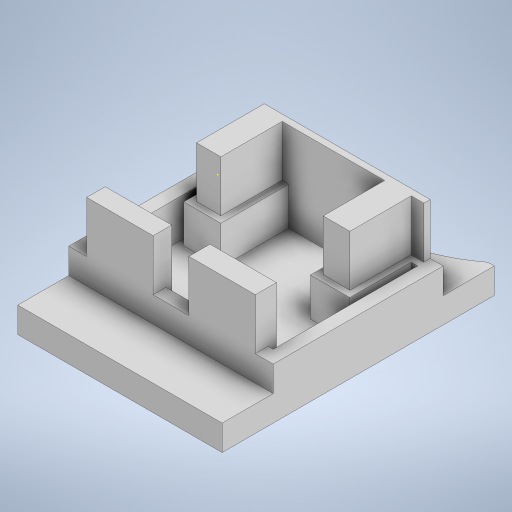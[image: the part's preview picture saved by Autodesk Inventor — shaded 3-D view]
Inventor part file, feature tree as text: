
AUTODESK INVENTOR PART (.ipt)
format: ipt  version: 2024 (Build 280153000, 153)  size: 340,480 bytes
history: native  units: mm
features: extrude x6, sketch x6, projected_geometry x1
ambient origin geometry x8: Origin, YZ Plane, XZ Plane, XY Plane, X Axis, Y Axis, Z Axis, Center Point
bodies: Solid1 (feature_tree)
feature tree (13):
  extrude  "Extrusion1"  Depth=160.0mm
  extrude  "Extrusion2"  Depth=25.0mm
  extrude  "Extrusion3"  Depth=40.0mm TaperAngle=0.0deg
  extrude  "Extrusion4"  Depth=20.0mm
  extrude  "Extrusion5"  Depth=80.0mm
  extrude  "Extrusion6"  Depth=40.0mm TaperAngle=0.0deg
  sketch  "Sketch7"  dims[d13=120.0mm d14=40.0mm d15=0.0mm d16=10.0mm d17=30.0mm d18=0.0mm d19=28.0mm d20=14.0mm d21=14.0mm d22=80.0mm d23=0.0mm d24=52.0mm d25=52.0mm d26=20.0mm d27=40.0mm d28=0.0mm d29=0.0mm d30=40.0mm d31=100.0mm d32=250.0mm d33=100.0mm d34=0.0mm d35=5.0mm]
  sketch  "Sketch1"  dims[d0=133.0mm d1=160.0mm]
  sketch  "Sketch2"  dims[d2=25.0mm d3=25.0mm]
  projected_geometry  "Projected Loop1"
  sketch  "Sketch4"  dims[d4=110.0mm d5=40.0mm d6=0.0mm]
  sketch  "Sketch5"  dims[d7=20.0mm d8=20.0mm]
  sketch  "Sketch6"  dims[d11=80.0mm d12=80.0mm]
